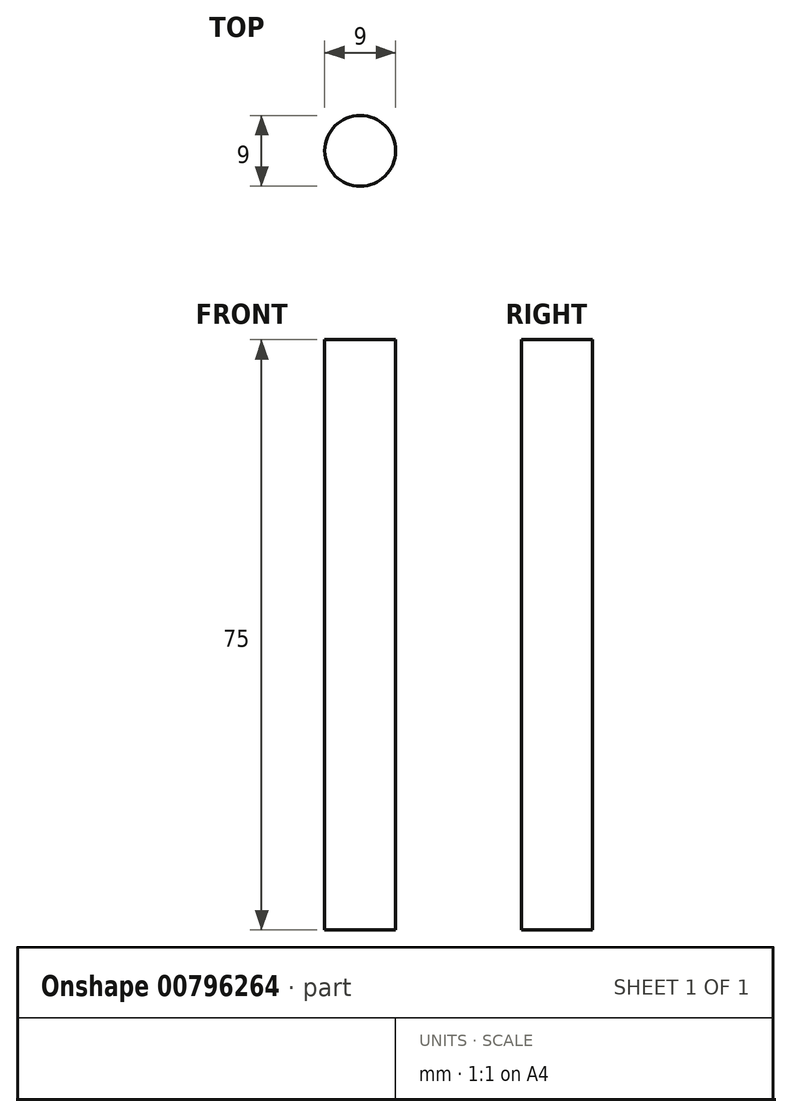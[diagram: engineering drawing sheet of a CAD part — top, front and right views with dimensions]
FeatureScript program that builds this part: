
annotation { "Feature Type Name" : "Feature", "Feature Type Description" : "" }
export const myFeature = defineFeature(function(context is Context, id is Id, definition is map)
    precondition{}
    {
        {
            var Q0;
            Q0=qCreatedBy(makeId("Top.planeOp"),FACE);
            var sketch = newSketch(context, id + "F0", { "sketchPlane" : qUnion([Q0])});
            skCircle(sketch, "E0", {"center": v(0, 0) * mm, "radius": 4.5 * mm});
            skSolve(sketch);
        }
        {
            var Q0;
            Q0 = qSketchRegion(id + "F0", true);
            extrude(context, id + "F1", {"entities" : qUnion([Q0]), "depth" : 75 * mm, "offsetDistance" : 25 * mm});
        }
    });
